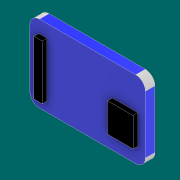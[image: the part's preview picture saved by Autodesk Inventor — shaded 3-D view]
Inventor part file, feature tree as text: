
AUTODESK INVENTOR PART (.ipt)
format: ipt  version: 2020 (Build 240168000, 168)  size: 108,544 bytes
history: native  units: mm
features: extrude x2, sketch x2, fillet x1
ambient origin geometry x8: Origin, YZ Plane, XZ Plane, XY Plane, X Axis, Y Axis, Z Axis, Center Point
bodies: Solid1 (feature_tree)
feature tree (5):
  extrude  "Extrusion1"  Depth=16.0mm
  fillet  "Fillet1"  Radius=2.0mm
  extrude  "Extrusion2"  Depth=1.0mm TaperAngle=0.0deg
  sketch  "Sketch1"  dims[d0=24.0mm d1=16.0mm d2=2.0mm d3=0.0mm]
  sketch  "Sketch2"  dims[d4=2.0mm d5=1.0mm d6=0.0mm]
